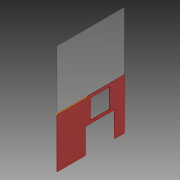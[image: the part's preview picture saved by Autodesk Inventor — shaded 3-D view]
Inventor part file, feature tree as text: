
AUTODESK INVENTOR PART (.ipt)
format: ipt  version: 2018 (Build 220112000, 112)  size: 147,968 bytes
history: native  units: in
note: dims shown in document units (in); Inventor stores cm internally (conversion verified against a paired STEP export)
features: plane x1, split x1, other x1
ambient origin geometry x8: Origin, YZ Plane, XZ Plane, XY Plane, X Axis, Y Axis, Z Axis, Center Point
bodies: Solid1 (feature_tree), Solid2 (feature_tree), Solid3 (feature_tree)
feature tree (3):
  plane  "Work Plane1"
  split  "Split2"
  other  "1_4 (0.25) Diameter Hole1"
